# Revit family: NBS_ConceptCubicleSystems_PnlCbclSym_OlympusGlass
name_source: partatom
category: Specialty Equipment
units: mm (PartAtom-declared; Revit-internal decimal feet)

## family parameters
Always vertical = Yes
Cut with Voids When Loaded = No
Part Type = Normal
Room Calculation Point = No
Round Connector Dimension = Use Diameter
Shared = No
Work Plane-Based = No

## types (8) — shared parameters
Application = Shower facilities in golf clubs, spas, health clubs and leisure centres
AssetType = Fixed
Category = Ss_25_12_60_60:Panel cubicle systems
Description = Olmypus glass cubicles
DoorLeafMaterial = NBS_ConceptCubicleSystems_ToughenedGlass
DurationUnit = year
Features = Polished edges, use of materials will help cope with the demands of high use shower facilities
FittingMaterial = NBS_ConceptCubicleSystems_MarineGradeStainlessSteel
Fittings = Marine grade stainless steel
GlassThickness = 10 mm  [stored 0.0328084 ft]
IfcExportAs = IfcFurnitureType
IfcExportType = USERDEFINED
IsBuiltIn = Yes
ManufacturerName = Concept Cubicle Systems
ManufacturerURL = www.conceptcubiclesystems.co.uk
Material = Toughened glass, stainless steel
ModelReference = Olympus Glass Cubicles
NBSCertification = www.nationalbimlibrary.com/cert/zrjpogql
NBSDescription = Panel cubicle system
NBSReference = 25-05-60/160
PanelSupports = 150 mm
Panels = 10 mm toughened glass
PartitionMaterial = NBS_ConceptCubicleSystems_ToughenedGlass
PilasterMaterial = NBS_ConceptCubicleSystems_ToughenedGlass
ProductInformation = https://www.conceptcubiclesystems.co.uk
Size = 1200 x 1950 mm
Status = UNSET
Style = Cubicle
SystemManufacturer = Concept Cubicle Systems
Uniclass2015Code = Ss_25_12_60_60
Uniclass2015Title = Panel cubicle systems
Uniclass2015Version = Systems v1.17
Version = 2
WarrantyDurationUnit = year

## per-type parameters (varying)
| type | BIMObjectName | HasFittingsLeft | HasFittingsRight | HasPartitionLeft | HasPartitionRight | HasPilasterPanelReturnLeft | HasPilasterPanelReturnRight | HasRailFront | HasRailRight | HasSupportPartitionLeft | HasSupportPartitionRight | IsEndCubicle | IsFirstCubicle | IsMiddleCubicle | IsSingleCubicle | IsWallEndEndCubicle | IsWallEndFirstCubicle | IsWallEndSingleCubicle | IsWallToWallSingleCubicle | Name | PilasterPanelReturnLeft | PilasterPanelReturnRight |
| SingleCubicle | NBS_ConceptCubicleSystems_PanelCubicleSystem_OlympusGlass_SingleCubicle | No | No | Yes | Yes | Yes | Yes | No | No | Yes | Yes | No | No | No | Yes | No | No | No | No | PanelCubicleSystem_OlympusGlass_SingleCubicle_ConceptCubicleSystems | 5 mm  [stored 0.0164042 ft] | 5 mm  [stored 0.0164042 ft] |
| WallToWallSingleCubicle | NBS_ConceptCubicleSystems_PanelCubicleSystem_OlympusGlass_WallToWallSingleCubicle | Yes | Yes | No | No | No | No | Yes | No | No | No | No | No | No | No | No | No | No | Yes | PanelCubicleSystem_OlympusGlass_WallToWallSingleCubicle_ConceptCubicleSystems | 0 mm  [stored 0 ft] | 0 mm  [stored 0 ft] |
| EndCubicle | NBS_ConceptCubicleSystems_PanelCubicleSystem_OlympusGlass_EndCubicle | No | No | No | Yes | No | Yes | No | Yes | No | Yes | Yes | No | No | No | No | No | No | No | PanelCubicleSystem_OlympusGlass_EndCubicle_ConceptCubicleSystems | 0 mm  [stored 0 ft] | 5 mm  [stored 0.0164042 ft] |
| FirstCubicle | NBS_ConceptCubicleSystems_PanelCubicleSystem_OlympusGlass_FirstCubicle | No | No | Yes | Yes | Yes | No | No | No | Yes | No | No | Yes | No | No | No | No | No | No | PanelCubicleSystem_OlympusGlass_FirstCubicle_ConceptCubicleSystems | 5 mm  [stored 0.0164042 ft] | 0 mm  [stored 0 ft] |
| WallEndFirstCubicle | NBS_ConceptCubicleSystems_PanelCubicleSystem_OlympusGlass_WallEndFirstCubicle | Yes | No | No | Yes | No | No | Yes | No | No | No | No | No | No | No | No | Yes | No | No | PanelCubicleSystem_OlympusGlass_WallEndFirstCubicle_ConceptCubicleSystems | 0 mm  [stored 0 ft] | 0 mm  [stored 0 ft] |
| WallEndSingleCubicle | NBS_ConceptCubicleSystems_PanelCubicleSystem_OlympusGlass_WallEndSingleCubicle | Yes | No | No | Yes | No | Yes | No | Yes | No | Yes | No | No | No | No | No | No | Yes | No | PanelCubicleSystem_OlympusGlass_WallEndSingleCubicle_ConceptCubicleSystems | 0 mm  [stored 0 ft] | 5 mm  [stored 0.0164042 ft] |
| MiddleCubicle | NBS_ConceptCubicleSystems_PanelCubicleSystem_OlympusGlass_MiddleCubicle | No | No | No | Yes | No | No | Yes | No | No | No | No | No | Yes | No | No | No | No | No | PanelCubicleSystem_OlympusGlass_MiddleCubicle_ConceptCubicleSystems | 0 mm  [stored 0 ft] | 0 mm  [stored 0 ft] |
| WallEndEndCubicle | NBS_ConceptCubicleSystems_PanelCubicleSystem_OlympusGlass_WallEndEndCubicle | No | Yes | No | No | No | No | Yes | No | No | No | No | No | No | No | Yes | No | No | No | PanelCubicleSystem_OlympusGlass_WallEndEndCubicle_ConceptCubicleSystems | 0 mm  [stored 0 ft] | 0 mm  [stored 0 ft] |

note: [stored X ft] marks values corroborated as IEEE doubles in the binary element streams (Revit-internal decimal feet)

## geometry (parser evidence)
native form markers: Sweep x9
no freeform markers — native parametric forms only
